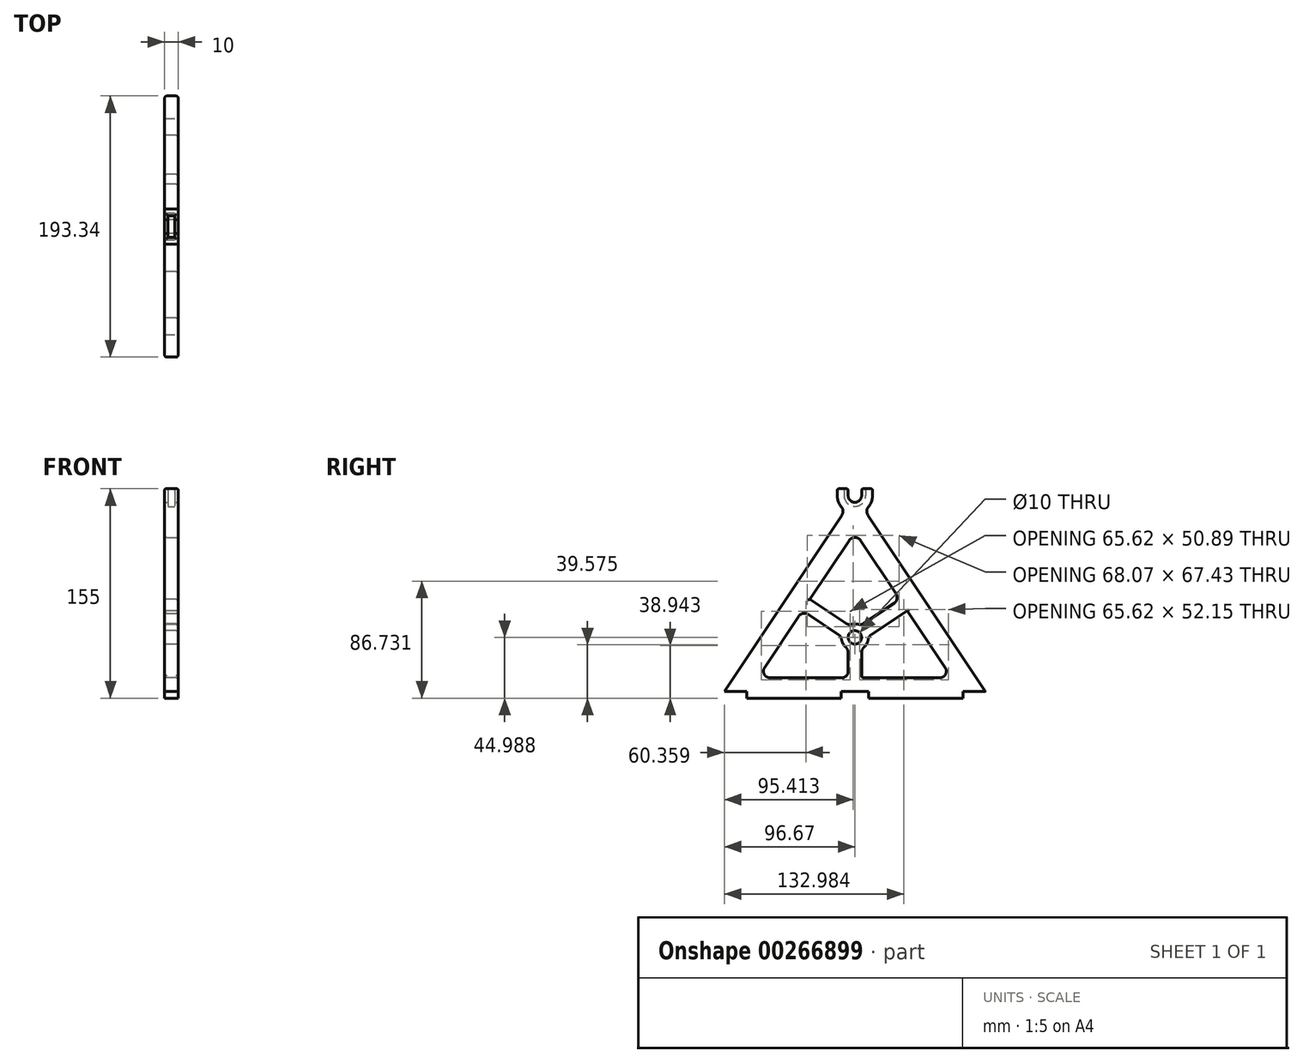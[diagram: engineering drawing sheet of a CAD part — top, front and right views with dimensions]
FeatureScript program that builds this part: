
annotation { "Feature Type Name" : "Feature", "Feature Type Description" : "" }
export const myFeature = defineFeature(function(context is Context, id is Id, definition is map)
    precondition{}
    {
        {
            var Q0;
            Q0=qCreatedBy(makeId("Right.planeOp"),FACE);
            var sketch = newSketch(context, id + "F0", { "sketchPlane" : qUnion([Q0])});
            skLineSegment(sketch, "E0", {"start": v(0, 0) * mm, "end": v(0, 150) * mm, "construction": true});
            skLineSegment(sketch, "E1", {"start": v(-100, 0) * mm, "end": v(100, 0) * mm});
            skLineSegment(sketch, "E2", {"start": v(-100, 0) * mm, "end": v(-7.24, 139.14) * mm});
            skLineSegment(sketch, "E3", {"start": v(100, 0) * mm, "end": v(7.24, 139.14) * mm});
            skCircle(sketch, "E4", {"center": v(0, 150) * mm, "radius": 8.05 * mm, "construction": true});
            skArc(sketch, "E5.0", {"start": v(7.24, 139.14) * mm, "mid": v(0, 163.05) * mm, "end": v(-7.24, 139.14) * mm});
            skLineSegment(sketch, "E6", {"start": v(-71.97, 15) * mm, "end": v(71.97, 15) * mm});
            skLineSegment(sketch, "E7", {"start": v(-71.97, 15) * mm, "end": v(0, 122.96) * mm});
            skLineSegment(sketch, "E8", {"start": v(0, 122.96) * mm, "end": v(71.97, 15) * mm});
            skSolve(sketch);
        }
        {
            var Q0;
            Q0=qSketchRegion(id+"F0",true);
            extrude(context, id + "F1", {"entities" : qUnion([Q0]), "depth" : 5 * mm, "hasSecondDirection" : true, "secondDirectionOppositeDirection" : true, "secondDirectionDepth" : 5 * mm});
        }
        {
            var Q0;
            Q0=qCreatedBy(makeId("Right.planeOp"),FACE);
            var sketch = newSketch(context, id + "F2", { "sketchPlane" : qUnion([Q0])});
            skArc(sketch, "E9", {"start": v(-8.05, 150) * mm, "mid": v(0, 141.95) * mm, "end": v(8.05, 150) * mm});
            skLineSegment(sketch, "E10", {"start": v(-8.05, 150) * mm, "end": v(8.05, 150) * mm, "construction": true});
            skLineSegment(sketch, "E11", {"start": v(8.05, 166.09) * mm, "end": v(-8.05, 166.09) * mm});
            skLineSegment(sketch, "E12", {"start": v(-8.05, 166.09) * mm, "end": v(-8.05, 150) * mm});
            skLineSegment(sketch, "E13", {"start": v(8.05, 150) * mm, "end": v(8.05, 166.09) * mm});
            skSolve(sketch);
        }
        {
            var Q0;
            Q0=qSketchRegion(id+"F2",true);
            extrude(context, id + "F3", {"entities" : qUnion([Q0]), "operationType" : NewBodyOperationType.REMOVE, "oppositeDirection" : true, "depth" : 2.55 * mm, "hasSecondDirection" : true, "secondDirectionOppositeDirection" : false, "secondDirectionDepth" : 2.55 * mm});
        }
        {
            var Q0;
            Q0=qCreatedBy(makeId("Right.planeOp"),FACE);
            var sketch = newSketch(context, id + "F4", { "sketchPlane" : qUnion([Q0])});
            skLineSegment(sketch, "E14.bottom", {"start": v(-26.82, 150) * mm, "end": v(26.82, 150) * mm});
            skLineSegment(sketch, "E14.top", {"start": v(-26.82, 166.63) * mm, "end": v(26.82, 166.63) * mm});
            skLineSegment(sketch, "E14.left", {"start": v(-26.82, 150) * mm, "end": v(-26.82, 166.63) * mm});
            skLineSegment(sketch, "E14.right", {"start": v(26.82, 150) * mm, "end": v(26.82, 166.63) * mm});
            skSolve(sketch);
        }
        {
            var Q0;
            Q0 = qSketchRegion(id + "F4", true);
            extrude(context, id + "F5", {"entities" : qUnion([Q0]), "operationType" : NewBodyOperationType.REMOVE, "endBound" : BoundingType.THROUGH_ALL, "oppositeDirection" : true, "depth" : 25 * mm, "hasSecondDirection" : true, "secondDirectionBound" : SecondDirectionBoundingType.THROUGH_ALL, "secondDirectionOppositeDirection" : false, "secondDirectionDepth" : 25 * mm});
        }
        {
            var Q0;
            Q0=qCreatedBy(makeId("Right.planeOp"),FACE);
            var sketch = newSketch(context, id + "F6", { "sketchPlane" : qUnion([Q0])});
            skCircle(sketch, "E15", {"center": v(0, 150) * mm, "radius": 5 * mm});
            skSolve(sketch);
        }
        {
            var Q0;
            Q0 = qSketchRegion(id + "F6", true);
            extrude(context, id + "F7", {"entities" : qUnion([Q0]), "operationType" : NewBodyOperationType.REMOVE, "endBound" : BoundingType.THROUGH_ALL, "oppositeDirection" : true, "depth" : 25 * mm, "hasSecondDirection" : true, "secondDirectionBound" : SecondDirectionBoundingType.THROUGH_ALL, "secondDirectionOppositeDirection" : false, "secondDirectionDepth" : 25 * mm});
        }
        {
            var Q0;
            Q0=makeQuery(id+"F7.boolean.opBoolean","SPLIT",FACE,{"disambiguationData":[OD(0.0)],"derivedFrom":makeQuery(id+"F5.boolean.opBoolean","COPY",FACE,{"derivedFrom":makeQuery(id+"F5.opExtrude","SWEPT_FACE",FACE,{"disambiguationData":[OSD([sQuery(id+"F4.wireOp",EDGE,"E14.bottom")])]})})});
            var Q1;
            Q1=makeQuery(id+"F7.boolean.opBoolean","SPLIT",FACE,{"disambiguationData":[OD(1.0)],"derivedFrom":makeQuery(id+"F5.boolean.opBoolean","COPY",FACE,{"derivedFrom":makeQuery(id+"F5.opExtrude","SWEPT_FACE",FACE,{"disambiguationData":[OSD([sQuery(id+"F4.wireOp",EDGE,"E14.bottom")])]})})});
            extrude(context, id + "F8", {"entities" : qUnion([Q0, Q1]), "operationType" : NewBodyOperationType.ADD, "depth" : 5 * mm});
        }
        {
            var Q0;
            Q0=makeQuery(id+"F3.boolean.opBoolean","COPY",FACE,{"derivedFrom":makeQuery(id+"F3.opExtrude","CAP_FACE",FACE,{"disambiguationData":[OSD([sQuery(id+"F2.wireOp",EDGE,"E9")])],"isStart":false})});
            var sketch = newSketch(context, id + "F9", { "sketchPlane" : qUnion([Q0])});
            skCircle(sketch, "E16", {"center": v(0, 150) * mm, "radius": 4.75 * mm});
            skSolve(sketch);
        }
        {
            var Q0;
            Q0=qSketchRegion(id+"F9",true);
            extrude(context, id + "F10", {"entities" : qUnion([Q0]), "operationType" : NewBodyOperationType.REMOVE, "endBound" : BoundingType.THROUGH_ALL, "oppositeDirection" : true, "depth" : 25 * mm});
        }
        {
            var Q0;
            Q0=makeQuery(id+"F1.opExtrude","CAP_FACE",FACE,{"disambiguationData":[OSD([sQuery(id+"F0.wireOp",EDGE,"E1"),sQuery(id+"F0.wireOp",EDGE,"E2"),sQuery(id+"F0.wireOp",EDGE,"E3"),sQuery(id+"F0.wireOp",EDGE,"E5.0"),sQuery(id+"F0.wireOp",EDGE,"E6"),sQuery(id+"F0.wireOp",EDGE,"E7"),sQuery(id+"F0.wireOp",EDGE,"E8")])],"isStart":false});
            var sketch = newSketch(context, id + "F11", { "sketchPlane" : qUnion([Q0])});
            skLineSegment(sketch, "E17.bottom", {"start": v(-10, 0) * mm, "end": v(10, 0) * mm});
            skLineSegment(sketch, "E17.top", {"start": v(-10, 5) * mm, "end": v(10, 5) * mm});
            skLineSegment(sketch, "E17.left", {"start": v(-10, 0) * mm, "end": v(-10, 5) * mm});
            skLineSegment(sketch, "E17.right", {"start": v(10, 0) * mm, "end": v(10, 5) * mm});
            skLineSegment(sketch, "E18.bottom", {"start": v(100, 0) * mm, "end": v(80, 0) * mm});
            skLineSegment(sketch, "E18.top", {"start": v(100, 5) * mm, "end": v(80, 5) * mm});
            skLineSegment(sketch, "E18.left", {"start": v(100, 0) * mm, "end": v(100, 5) * mm});
            skLineSegment(sketch, "E18.right", {"start": v(80, 0) * mm, "end": v(80, 5) * mm});
            skLineSegment(sketch, "E19.bottom", {"start": v(-100, 0) * mm, "end": v(-80, 0) * mm});
            skLineSegment(sketch, "E19.top", {"start": v(-100, 5) * mm, "end": v(-80, 5) * mm});
            skLineSegment(sketch, "E19.left", {"start": v(-100, 0) * mm, "end": v(-100, 5) * mm});
            skLineSegment(sketch, "E19.right", {"start": v(-80, 0) * mm, "end": v(-80, 5) * mm});
            skSolve(sketch);
        }
        {
            var Q0;
            Q0=qSketchRegion(id+"F11",true);
            extrude(context, id + "F12", {"entities" : qUnion([Q0]), "operationType" : NewBodyOperationType.REMOVE, "endBound" : BoundingType.THROUGH_ALL, "oppositeDirection" : true, "depth" : 25 * mm});
        }
        {
            var Q0;
            Q0=qCreatedBy(makeId("Right.planeOp"),FACE);
            var sketch = newSketch(context, id + "F13", { "sketchPlane" : qUnion([Q0])});
            skLineSegment(sketch, "E20", {"start": v(-35.99, 68.98) * mm, "end": v(0, 44.99) * mm, "construction": true});
            skLineSegment(sketch, "E21", {"start": v(0, 44.99) * mm, "end": v(35.99, 68.98) * mm, "construction": true});
            skLineSegment(sketch, "E22", {"start": v(0, 44.99) * mm, "end": v(0, 15) * mm, "construction": true});
            skCircle(sketch, "E23", {"center": v(0, 44.99) * mm, "radius": 5 * mm});
            skArc(sketch, "E24.0", {"start": v(4.43, 53.95) * mm, "mid": v(0, 54.99) * mm, "end": v(-4.43, 53.95) * mm});
            skLineSegment(sketch, "E25.0", {"start": v(-38.76, 64.82) * mm, "end": v(-9.98, 45.63) * mm});
            skLineSegment(sketch, "E26.0", {"start": v(-33.21, 73.14) * mm, "end": v(-4.43, 53.95) * mm});
            skLineSegment(sketch, "E27.0", {"start": v(9.98, 45.63) * mm, "end": v(38.76, 64.82) * mm});
            skLineSegment(sketch, "E28.0", {"start": v(4.43, 53.95) * mm, "end": v(33.21, 73.14) * mm});
            skLineSegment(sketch, "E29.0", {"start": v(-5, 36.33) * mm, "end": v(-5, 15) * mm});
            skLineSegment(sketch, "E30", {"start": v(-38.76, 64.82) * mm, "end": v(-33.21, 73.14) * mm});
            skLineSegment(sketch, "E31", {"start": v(33.21, 73.14) * mm, "end": v(38.76, 64.82) * mm});
            skLineSegment(sketch, "E32", {"start": v(5, 15) * mm, "end": v(-5, 15) * mm});
            skArc(sketch, "E33.trimOffspring", {"start": v(-9.98, 45.63) * mm, "mid": v(-8.82, 40.27) * mm, "end": v(-5, 36.33) * mm});
            skArc(sketch, "E34.trimOffspring", {"start": v(5, 36.33) * mm, "mid": v(8.82, 40.27) * mm, "end": v(9.98, 45.63) * mm});
            skLineSegment(sketch, "E35.trimOffspring", {"start": v(5, 36.33) * mm, "end": v(5, 15) * mm});
            skSolve(sketch);
        }
        {
            var Q0;
            Q0=qSketchRegion(id+"F13",true);
            extrude(context, id + "F14", {"entities" : qUnion([Q0]), "operationType" : NewBodyOperationType.ADD, "depth" : 5 * mm, "hasSecondDirection" : true, "secondDirectionOppositeDirection" : true, "secondDirectionDepth" : 5 * mm});
        }
        {
            var Q0;
            Q0=makeQuery(id+"F1.opExtrude","SWEPT_EDGE",EDGE,{"disambiguationData":[OSD([sQuery(id+"F0.wireOp",EDGE,"E2"),sQuery(id+"F0.wireOp",EDGE,"E5.0")])]});
            var Q1;
            Q1=makeQuery(id+"F1.opExtrude","SWEPT_EDGE",EDGE,{"disambiguationData":[OSD([sQuery(id+"F0.wireOp",EDGE,"E3"),sQuery(id+"F0.wireOp",EDGE,"E5.0")])]});
            var Q2;
            Q2=makeQuery(id+"F1.opExtrude","SWEPT_EDGE",EDGE,{"disambiguationData":[OSD([sQuery(id+"F0.wireOp",EDGE,"E6"),sQuery(id+"F0.wireOp",EDGE,"E8")])]});
            var Q3;
            Q3=makeQuery(id+"F1.opExtrude","SWEPT_EDGE",EDGE,{"disambiguationData":[OSD([sQuery(id+"F0.wireOp",EDGE,"E7"),sQuery(id+"F0.wireOp",EDGE,"E8")])]});
            var Q4;
            Q4=makeQuery(id+"F1.opExtrude","SWEPT_EDGE",EDGE,{"disambiguationData":[OSD([sQuery(id+"F0.wireOp",EDGE,"E6"),sQuery(id+"F0.wireOp",EDGE,"E7")])]});
            var Q5;
            Q5=makeQuery(id+"F14.opExtrude","SWEPT_EDGE",EDGE,{"disambiguationData":[OSD([sQuery(id+"F13.wireOp",EDGE,"E26.0"),sQuery(id+"F13.wireOp",EDGE,"E30")])]});
            var Q6;
            Q6=makeQuery(id+"F14.opExtrude","SWEPT_EDGE",EDGE,{"disambiguationData":[OSD([sQuery(id+"F13.wireOp",EDGE,"E25.0"),sQuery(id+"F13.wireOp",EDGE,"E30")])]});
            var Q7;
            Q7=makeQuery(id+"F14.opExtrude","SWEPT_EDGE",EDGE,{"disambiguationData":[OSD([sQuery(id+"F13.wireOp",EDGE,"E27.0"),sQuery(id+"F13.wireOp",EDGE,"E31")])]});
            var Q8;
            Q8=makeQuery(id+"F14.opExtrude","SWEPT_EDGE",EDGE,{"disambiguationData":[OSD([sQuery(id+"F13.wireOp",EDGE,"E25.0"),sQuery(id+"F13.wireOp",EDGE,"E33.trimOffspring")])]});
            var Q9;
            Q9=makeQuery(id+"F14.opExtrude","SWEPT_EDGE",EDGE,{"disambiguationData":[OSD([sQuery(id+"F13.wireOp",EDGE,"E29.0"),sQuery(id+"F13.wireOp",EDGE,"E33.trimOffspring")])]});
            var Q10;
            Q10=makeQuery(id+"F14.opExtrude","SWEPT_EDGE",EDGE,{"disambiguationData":[OSD([sQuery(id+"F13.wireOp",EDGE,"E34.trimOffspring"),sQuery(id+"F13.wireOp",EDGE,"E35.trimOffspring")])]});
            var Q11;
            Q11=makeQuery(id+"F14.opExtrude","SWEPT_EDGE",EDGE,{"disambiguationData":[OSD([sQuery(id+"F13.wireOp",EDGE,"E27.0"),sQuery(id+"F13.wireOp",EDGE,"E34.trimOffspring")])]});
            var Q12;
            Q12=makeQuery(id+"F14.opExtrude","SWEPT_EDGE",EDGE,{"disambiguationData":[OSD([sQuery(id+"F13.wireOp",EDGE,"E28.0"),sQuery(id+"F13.wireOp",EDGE,"E24.0")])]});
            var Q13;
            Q13=makeQuery(id+"F14.opExtrude","SWEPT_EDGE",EDGE,{"disambiguationData":[OSD([sQuery(id+"F13.wireOp",EDGE,"E26.0"),sQuery(id+"F13.wireOp",EDGE,"E24.0")])]});
            var Q14;
            Q14=makeQuery(id+"F14.opExtrude","SWEPT_EDGE",EDGE,{"disambiguationData":[OSD([sQuery(id+"F13.wireOp",EDGE,"E28.0"),sQuery(id+"F13.wireOp",EDGE,"E31")])]});
            var Q15;
            Q15=makeQuery(id+"F14.opExtrude","SWEPT_EDGE",EDGE,{"disambiguationData":[OSD([sQuery(id+"F13.wireOp",EDGE,"E29.0"),sQuery(id+"F13.wireOp",EDGE,"E32")])]});
            var Q16;
            Q16=makeQuery(id+"F14.opExtrude","SWEPT_EDGE",EDGE,{"disambiguationData":[OSD([sQuery(id+"F13.wireOp",EDGE,"E32"),sQuery(id+"F13.wireOp",EDGE,"E35.trimOffspring")])]});
            fillet(context, id + "F15", {"entities" : qUnion([Q0, Q1, Q2, Q3, Q4, Q5, Q6, Q7, Q8, Q9, Q10, Q11, Q12, Q13, Q14, Q15, Q16]), "radius" : 5 * mm, "tangentPropagation" : true, "allowEdgeOverflow" : false});
        }
        {
            var Q0;
            Q0=makeQuery(id+"F14.opExtrude","SWEPT_FACE",FACE,{"disambiguationData":[OSD([sQuery(id+"F13.wireOp",EDGE,"E28.0")])]});
            var Q1;
            Q1=makeQuery(id+"F14.opExtrude","SWEPT_FACE",FACE,{"disambiguationData":[OSD([sQuery(id+"F13.wireOp",EDGE,"E23")])]});
            var Q2;
            {var subQ0=sQuery(id+"F0.wireOp",EDGE,"E8");var subQ4=sQuery(id+"F0.wireOp",EDGE,"E6");Q2=makeQuery(id+"F14.boolean.opBoolean","SPLIT",FACE,{"disambiguationData":[TD([makeQuery(id+"F1.opExtrude","SWEPT_FACE",FACE,{"disambiguationData":[OSD([subQ0])]})])],"derivedFrom":makeQuery(id+"F1.opExtrude","SWEPT_FACE",FACE,{"disambiguationData":[OSD([subQ4])]})});}
            var Q3;
            Q3=makeQuery(id+"F1.opExtrude","CAP_EDGE",EDGE,{"disambiguationData":[OSD([sQuery(id+"F0.wireOp",EDGE,"E2")])],"isStart":false});
            var Q4;
            Q4=makeQuery(id+"F1.opExtrude","CAP_EDGE",EDGE,{"disambiguationData":[OSD([sQuery(id+"F0.wireOp",EDGE,"E2")])],"isStart":true});
            var Q5;
            Q5=makeQuery(id+"F1.opExtrude","CAP_EDGE",EDGE,{"disambiguationData":[OSD([sQuery(id+"F0.wireOp",EDGE,"E3")])],"isStart":false});
            var Q6;
            Q6=makeQuery(id+"F1.opExtrude","CAP_EDGE",EDGE,{"disambiguationData":[OSD([sQuery(id+"F0.wireOp",EDGE,"E3")])],"isStart":true});
            var Q7;
            {var subQ3=sQuery(id+"F0.wireOp",EDGE,"E7");var subQ4=sQuery(id+"F0.wireOp",EDGE,"E6");Q7=makeQuery(id+"F14.boolean.opBoolean","SPLIT",FACE,{"disambiguationData":[TD([makeQuery(id+"F1.opExtrude","SWEPT_FACE",FACE,{"disambiguationData":[OSD([subQ3])]})])],"derivedFrom":makeQuery(id+"F1.opExtrude","SWEPT_FACE",FACE,{"disambiguationData":[OSD([subQ4])]})});}
            fillet(context, id + "F16", {"entities" : qUnion([Q0, Q1, Q2, Q3, Q4, Q5, Q6, Q7]), "radius" : 1.5 * mm, "tangentPropagation" : true, "allowEdgeOverflow" : false});
        }
        {
            var Q0;
            {var subQ0=sQuery(id+"F4.wireOp",EDGE,"E14.bottom");Q0=makeQuery(id+"F8.opExtrude","CAP_FACE",FACE,{"disambiguationData":[OSD([subQ0]),TDD([makeQuery(id+"F7.boolean.opBoolean","SPLIT",FACE,{"disambiguationData":[OD(0.0)],"derivedFrom":makeQuery(id+"F5.boolean.opBoolean","COPY",FACE,{"derivedFrom":makeQuery(id+"F5.opExtrude","SWEPT_FACE",FACE,{"disambiguationData":[OSD([subQ0])]})})})])],"isStart":false});}
            var Q1;
            {var subQ0=sQuery(id+"F4.wireOp",EDGE,"E14.bottom");Q1=makeQuery(id+"F8.opExtrude","CAP_FACE",FACE,{"disambiguationData":[OSD([subQ0]),TDD([makeQuery(id+"F7.boolean.opBoolean","SPLIT",FACE,{"disambiguationData":[OD(1.0)],"derivedFrom":makeQuery(id+"F5.boolean.opBoolean","COPY",FACE,{"derivedFrom":makeQuery(id+"F5.opExtrude","SWEPT_FACE",FACE,{"disambiguationData":[OSD([subQ0])]})})})])],"isStart":false});}
            fillet(context, id + "F17", {"entities" : qUnion([Q0, Q1]), "radius" : 1 * mm, "tangentPropagation" : true, "allowEdgeOverflow" : false});
        }
    });
